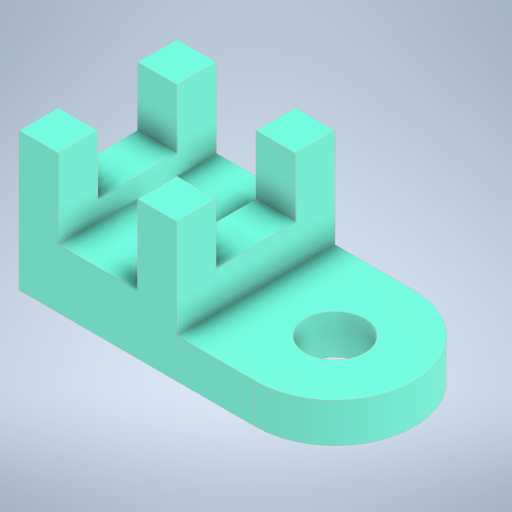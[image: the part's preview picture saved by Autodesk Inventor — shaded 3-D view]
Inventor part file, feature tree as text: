
AUTODESK INVENTOR PART (.ipt)
format: ipt  version: 2024 (Build 280153000, 153)  size: 286,720 bytes
history: native  units: in
note: dims shown in document units (in); Inventor stores cm internally (conversion verified against a paired STEP export)
features: extrude x4, other x4
ambient origin geometry x8: Origin, YZ Plane, XZ Plane, XY Plane, X Axis, Y Axis, Z Axis, Center Point
bodies: Solid1 (feature_tree)
feature tree (8):
  extrude  "SIDE PROFILE EXTRUSION"  Depth=3.0in
  extrude  "FRONT ROUNDING"  Depth=1.5in
  extrude  "HOLE CUTOUT"  Depth=1.75in
  extrude  "RECTANGULAR CUTOUT"  Depth=0.5in
  other  "SIDE PROFILE"
  other  "SEMICIRCLE"
  other  "CIRCLE"
  other  "RECTANGLE"
